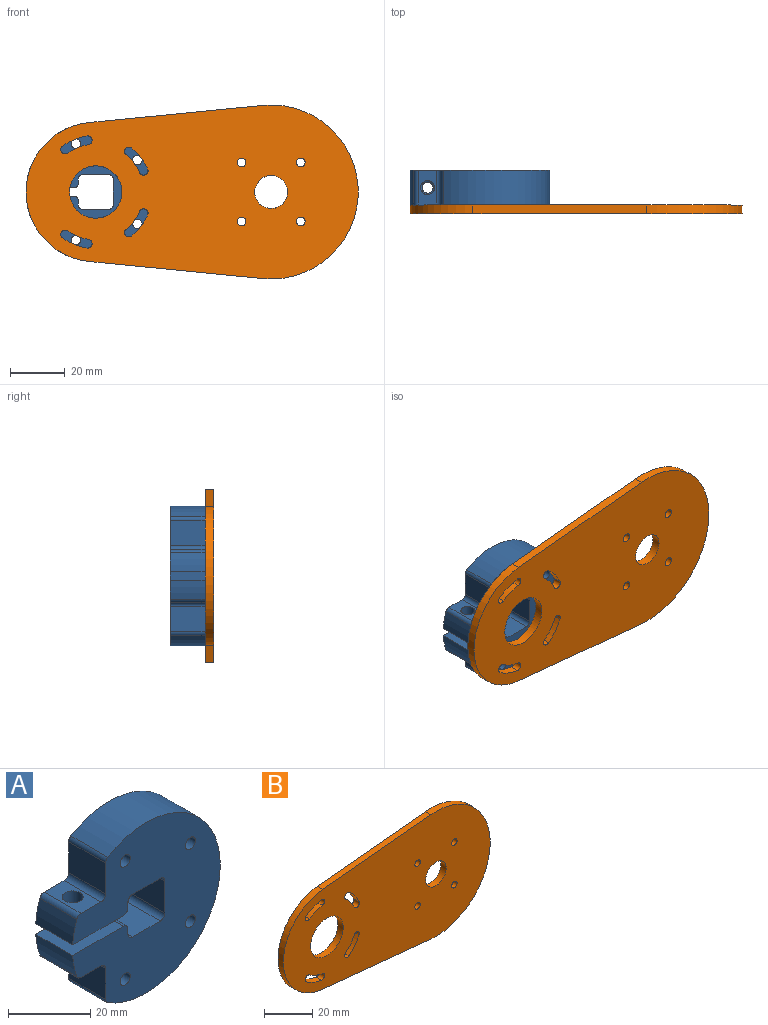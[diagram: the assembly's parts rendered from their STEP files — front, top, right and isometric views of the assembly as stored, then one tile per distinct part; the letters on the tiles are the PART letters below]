
ASSEMBLY  parts=2 mates=1
PART A: 35 faces, bbox 50.8x12.7x50.8 mm
  f0: cylinder r=25.4mm len=12.7mm, axis (0,1,0), area 89.5mm2, adj f2,f3,f11,f19
  f1: cylinder r=25.4mm len=50.8mm, axis (0,1,0), area 1367.9mm2, adj f2,f3,f18,f20
  f2: plane 50.8x50.75mm, normal (0,-1,0), area 1635.1mm2, adj f0,f1,f4,f5,f6,f7,f8,f9
  f3: plane 50.8x50.75mm, normal (0,1,0), area 1635.1mm2, adj f0,f1,f4,f5,f6,f7,f8,f9
  f4: cylinder r=25.4mm len=12.7mm, axis (0,1,0), area 89.5mm2, adj f2,f3,f5,f17
  f5: plane 17.41x12.7mm, normal (0,0,1), area 208.3mm2, adj f2,f3,f4,f22,f34
  f6: plane 12.7x1.59mm, normal (1,0,0), area 20.2mm2, adj f2,f3,f22,f24
  f7: plane 12.7x9.53mm, normal (0,0,1), area 121mm2, adj f2,f3,f24,f25
  f8: plane 12.7x9.53mm, normal (-1,0,0), area 121mm2, adj f2,f3,f25,f26
  f9: plane 12.7x9.53mm, normal (0,0,-1), area 121mm2, adj f2,f3,f26,f27
  f10: plane 12.7x1.59mm, normal (1,0,0), area 20.2mm2, adj f2,f3,f23,f27
  f11: plane 17.41x12.7mm, normal (0,0,-1), area 208.4mm2, adj f0,f2,f3,f23,f32
  f12: plane 12.7x9.2mm, normal (-1,0,0), area 116.8mm2, adj f2,f3,f16,f18
  f13: plane 12.7x6.84mm, normal (0,0,-1), area 74.1mm2, adj f2,f3,f16,f17,f34
  f14: plane 12.7x6.84mm, normal (0,0,1), area 66.6mm2, adj f2,f3,f19,f21,f33
  f15: plane 12.7x9.2mm, normal (-1,0,0), area 116.8mm2, adj f2,f3,f20,f21
  f16: cylinder r=1.59mm len=12.7mm, axis (0,-1,0), area 31.7mm2, adj f2,f3,f12,f13
  f17: cylinder r=1.59mm len=12.7mm, axis (0,1,0), area 24.8mm2, adj f2,f3,f4,f13
  f18: cylinder r=1.59mm len=12.7mm, axis (0,1,0), area 20.6mm2, adj f1,f2,f3,f12
  f19: cylinder r=1.59mm len=12.7mm, axis (0,1,0), area 24.8mm2, adj f0,f2,f3,f14
  f20: cylinder r=1.59mm len=12.7mm, axis (0,1,0), area 20.6mm2, adj f1,f2,f3,f15
  f21: cylinder r=1.59mm len=12.7mm, axis (0,-1,0), area 31.7mm2, adj f2,f3,f14,f15
  f22: cylinder r=1.59mm len=12.7mm, axis (0,1,0), area 31.7mm2, adj f2,f3,f5,f6
  f23: cylinder r=1.59mm len=12.7mm, axis (0,-1,0), area 31.7mm2, adj f2,f3,f10,f11
  f24: cylinder r=1.59mm len=12.7mm, axis (0,1,0), area 31.7mm2, adj f2,f3,f6,f7
  f25: cylinder r=1.59mm len=12.7mm, axis (0,-1,0), area 31.7mm2, adj f2,f3,f7,f8
  f26: cylinder r=1.59mm len=12.7mm, axis (0,1,0), area 31.7mm2, adj f2,f3,f8,f9
  f27: cylinder r=1.59mm len=12.7mm, axis (0,-1,0), area 31.7mm2, adj f2,f3,f9,f10
  f28: cylinder r=1.73mm len=12.7mm, axis (0,-1,0), area 137.8mm2, adj f2,f3
  f29: cylinder r=1.73mm len=12.7mm, axis (0,-1,0), area 137.8mm2, adj f2,f3
  f30: cylinder r=1.73mm len=12.7mm, axis (0,-1,0), area 137.8mm2, adj f2,f3
  f31: cylinder r=1.73mm len=12.7mm, axis (0,-1,0), area 137.8mm2, adj f2,f3
  f32: cone r=0mm half-angle=59deg, axis (0,0,1), area 8.8mm2, adj f11,f33
  f33: cylinder r=2.54mm len=7.62mm, axis (0,0,1), area 121.6mm2, adj f14,f32
  f34: cylinder r=2.02mm len=7.94mm, axis (0,0,-1), area 100.7mm2, adj f5,f13
PART B: 28 faces, bbox 120.9x3.2x63.3 mm
  f0: cylinder r=25.4mm len=50.56mm, axis (0,1,0), area 237.5mm2, adj f1,f3,f4,f5
  f1: plane 63.19x6.22mm, normal (-0.1,0,-1), area 201.6mm2, adj f0,f2,f4,f5
  f2: cylinder r=31.65mm len=63.3mm, axis (0,1,0), area 335.4mm2, adj f1,f3,f4,f5
  f3: plane 63.19x6.22mm, normal (-0.1,0,1), area 201.6mm2, adj f0,f2,f4,f5
  f4: plane 120.86x63.3mm, normal (0,-1,0), area 5669.6mm2, adj f0,f1,f2,f3,f6,f7,f8,f9
  f5: plane 120.86x63.3mm, normal (0,1,0), area 5669.6mm2, adj f0,f1,f2,f3,f6,f7,f8,f9
  f6: cylinder r=6mm len=12mm, axis (0,-1,0), area 119.7mm2, adj f4,f5
  f7: cylinder r=9.53mm len=19.05mm, axis (0,-1,0), area 190mm2, adj f4,f5
  f8: cylinder r=1.59mm len=3.18mm, axis (0,-1,0), area 31.7mm2, adj f4,f5
  f9: cylinder r=1.59mm len=3.18mm, axis (0,-1,0), area 31.7mm2, adj f4,f5
  f10: cylinder r=1.59mm len=3.18mm, axis (0,-1,0), area 31.7mm2, adj f4,f5
  f11: cylinder r=1.59mm len=3.18mm, axis (0,-1,0), area 31.7mm2, adj f4,f5
  f12: cylinder r=1.59mm len=3.18mm, axis (0,-1,0), area 15.8mm2, adj f4,f5,f13,f15
  f13: cylinder r=20.64mm len=8.9mm, axis (0,-1,0), area 30.9mm2, adj f4,f5,f12,f14
  f14: cylinder r=1.59mm len=3.18mm, axis (0,-1,0), area 15.8mm2, adj f4,f5,f13,f15
  f15: cylinder r=17.46mm len=7.53mm, axis (0,-1,0), area 26.1mm2, adj f4,f5,f12,f14
  f16: cylinder r=1.59mm len=3.18mm, axis (0,-1,0), area 15.8mm2, adj f4,f5,f17,f19
  f17: cylinder r=20.64mm len=7.65mm, axis (0,-1,0), area 30.9mm2, adj f4,f5,f16,f18
  f18: cylinder r=1.59mm len=3.18mm, axis (0,-1,0), area 15.8mm2, adj f4,f5,f17,f19
  f19: cylinder r=17.46mm len=6.47mm, axis (0,-1,0), area 26.1mm2, adj f4,f5,f16,f18
  f20: cylinder r=1.59mm len=3.18mm, axis (0,-1,0), area 15.8mm2, adj f4,f5,f21,f23
  f21: cylinder r=20.64mm len=7.65mm, axis (0,-1,0), area 30.9mm2, adj f4,f5,f20,f22
  f22: cylinder r=1.59mm len=3.18mm, axis (0,-1,0), area 15.8mm2, adj f4,f5,f21,f23
  f23: cylinder r=17.46mm len=6.47mm, axis (0,-1,0), area 26.1mm2, adj f4,f5,f20,f22
  f24: cylinder r=1.59mm len=3.18mm, axis (0,-1,0), area 15.8mm2, adj f4,f5,f25,f27
  f25: cylinder r=20.64mm len=8.9mm, axis (0,-1,0), area 30.9mm2, adj f4,f5,f24,f26
  f26: cylinder r=1.59mm len=3.18mm, axis (0,-1,0), area 15.8mm2, adj f4,f5,f25,f27
  f27: cylinder r=17.46mm len=7.53mm, axis (0,-1,0), area 26.1mm2, adj f4,f5,f24,f26
PLACE A t=(-0.09,7.99,0.4)mm
PLACE B t=(-0.09,0.05,0.4)mm fixed
MATE cylindrical A.f0 <-> B.f0  axis (0,1,0) through (-0.09,1.64,0.4)mm
